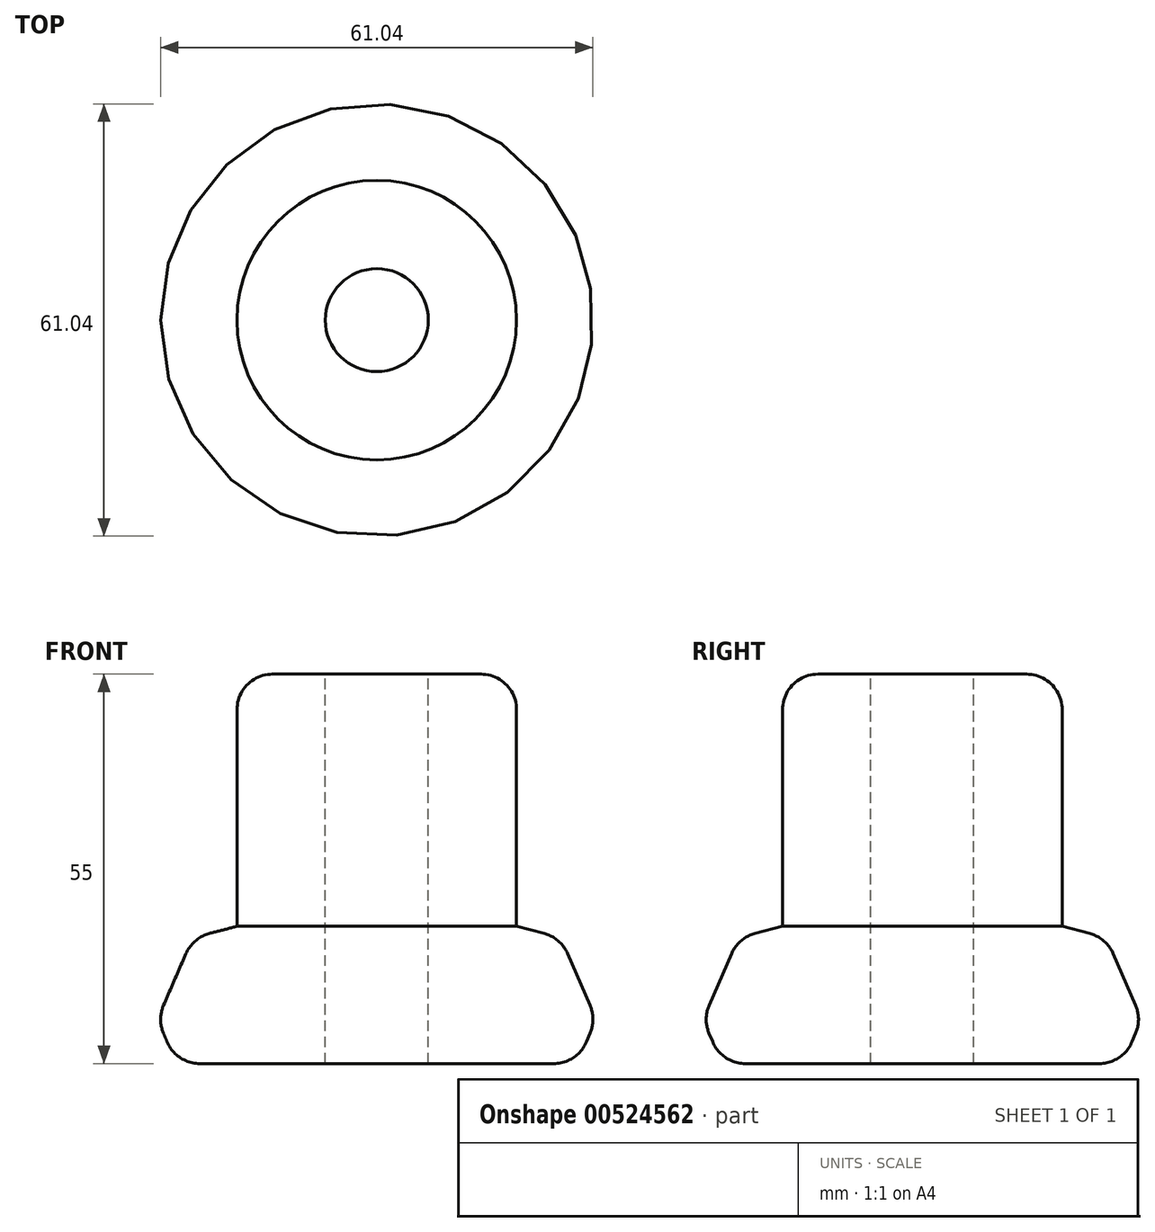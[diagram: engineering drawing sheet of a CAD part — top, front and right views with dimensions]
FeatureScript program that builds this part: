
annotation { "Feature Type Name" : "Feature", "Feature Type Description" : "" }
export const myFeature = defineFeature(function(context is Context, id is Id, definition is map)
    precondition{}
    {
        {
            var Q0;
            Q0=qCreatedBy(makeId("Front.planeOp"),FACE);
            var sketch = newSketch(context, id + "F0", { "sketchPlane" : qUnion([Q0])});
            skLineSegment(sketch, "E0", {"start": v(0, 48.73) * mm, "end": v(14.74, 48.73) * mm});
            skLineSegment(sketch, "E1", {"start": v(19.74, 43.73) * mm, "end": v(19.74, 13.11) * mm});
            skLineSegment(sketch, "E2", {"start": v(19.74, 13.11) * mm, "end": v(23.61, 12.1) * mm});
            skLineSegment(sketch, "E3", {"start": v(26.95, 9.26) * mm, "end": v(30.11, 1.96) * mm});
            skLineSegment(sketch, "E4", {"start": v(30.13, -1.97) * mm, "end": v(29.6, -3.21) * mm});
            skLineSegment(sketch, "E5", {"start": v(25, -6.27) * mm, "end": v(0, -6.27) * mm});
            skLineSegment(sketch, "E6", {"start": v(0, -6.27) * mm, "end": v(0, 48.73) * mm});
            skPoint(sketch, "E7.visualSharp", {"position": v(19.74, 48.73) * mm});
            skArc(sketch, "E7.filletArc", {"start": v(19.74, 43.73) * mm, "mid": v(18.27, 47.26) * mm, "end": v(14.74, 48.73) * mm});
            skPoint(sketch, "E8.visualSharp", {"position": v(25.98, 11.5) * mm});
            skArc(sketch, "E8.filletArc", {"start": v(26.95, 9.26) * mm, "mid": v(25.6, 11.07) * mm, "end": v(23.61, 12.1) * mm});
            skPoint(sketch, "E9.visualSharp", {"position": v(30.96, 0) * mm});
            skArc(sketch, "E9.filletArc", {"start": v(30.13, -1.97) * mm, "mid": v(30.52, 0) * mm, "end": v(30.11, 1.96) * mm});
            skPoint(sketch, "E10.visualSharp", {"position": v(28.32, -6.27) * mm});
            skArc(sketch, "E10.filletArc", {"start": v(25, -6.27) * mm, "mid": v(27.77, -5.44) * mm, "end": v(29.6, -3.21) * mm});
            skSolve(sketch);
        }
        {
            var Q0;
            Q0=makeQuery(id+"F0.imprint","IMPRINT",FACE,{"disambiguationData":[TD([[makeQuery(id+"F0.imprint","IMPRINT",EDGE,{"derivedFrom":sQuery(id+"F0.wireOp",EDGE,"E0")}),-1.0]])]});
            var Q1;
            Q1=sQuery(id+"F0.wireOp",EDGE,"E6");
            revolve(context, id + "F1", {"entities" : qUnion([Q0]), "axis" : qUnion([Q1]), "revolveType" : RevolveType.FULL});
        }
        {
            var Q0;
            Q0=makeQuery(id+"F1.opRevolve","SWEPT_FACE",FACE,{"disambiguationData":[OSD([sQuery(id+"F0.wireOp",EDGE,"E0")])]});
            var sketch = newSketch(context, id + "F2", { "sketchPlane" : qUnion([Q0])});
            skCircle(sketch, "E11", {"center": v(0, 0) * mm, "radius": 7.27 * mm});
            skSolve(sketch);
        }
        {
            var Q0;
            Q0=makeQuery(id+"F2.imprint","IMPRINT",FACE,{"disambiguationData":[TD([[makeQuery(id+"F2.imprint","IMPRINT",EDGE,{"derivedFrom":sQuery(id+"F2.wireOp",EDGE,"E11")}),1.0]])]});
            extrude(context, id + "F3", {"entities" : qUnion([Q0]), "operationType" : NewBodyOperationType.REMOVE, "endBound" : BoundingType.THROUGH_ALL, "oppositeDirection" : true, "depth" : 25 * mm, "offsetDistance" : 25 * mm});
        }
    });
